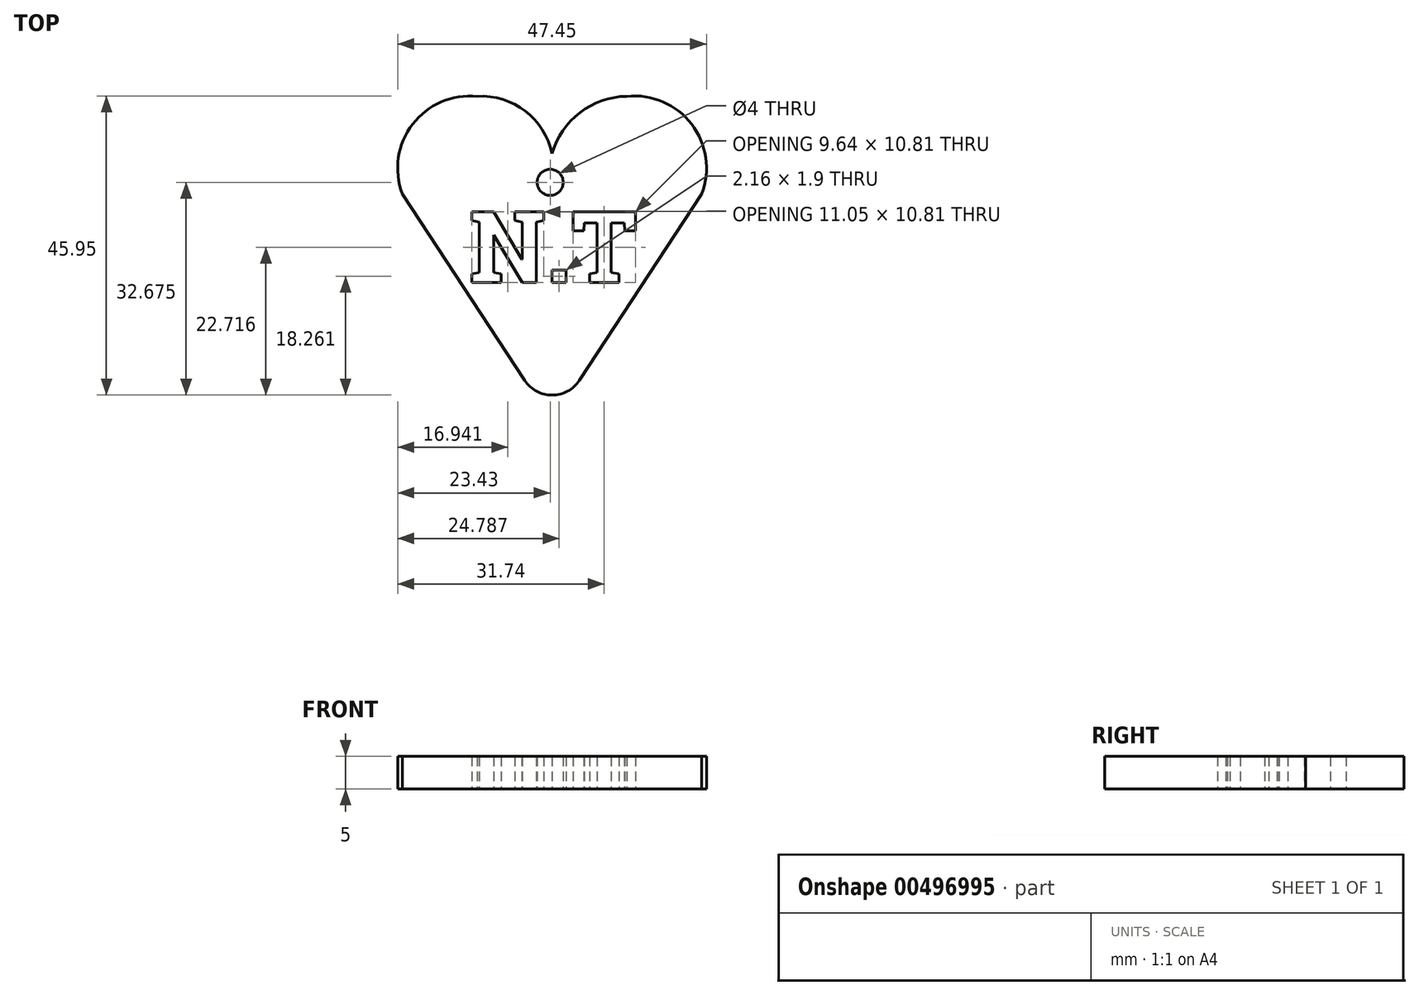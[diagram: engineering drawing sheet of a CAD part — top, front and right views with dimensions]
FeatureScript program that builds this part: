
annotation { "Feature Type Name" : "Feature", "Feature Type Description" : "" }
export const myFeature = defineFeature(function(context is Context, id is Id, definition is map)
    precondition{}
    {
        {
            var Q0;
            Q0=qCreatedBy(makeId("Top.planeOp"),FACE);
            var sketch = newSketch(context, id + "F0", { "sketchPlane" : qUnion([Q0])});
            skPoint(sketch, "E0.startSnap0", {"position": v(-11.21, 33.91) * mm});
            skLineSegment(sketch, "E1", {"start": v(-22.71, 18.92) * mm, "end": v(-3.9, -9.73) * mm});
            skLineSegment(sketch, "E2", {"start": v(23.29, 18.92) * mm, "end": v(4.47, -9.73) * mm});
            skPoint(sketch, "E3.visualSharp", {"position": v(0.29, -16.09) * mm});
            skArc(sketch, "E3.filletArc", {"start": v(-3.9, -9.73) * mm, "mid": v(0.29, -11.98) * mm, "end": v(4.47, -9.73) * mm});
            skArc(sketch, "E4", {"start": v(0.29, 25.1) * mm, "mid": v(-3.83, 31.63) * mm, "end": v(-11.21, 33.91) * mm});
            skArc(sketch, "E5", {"start": v(11.79, 33.91) * mm, "mid": v(4.58, 31.4) * mm, "end": v(0.29, 25.1) * mm});
            skArc(sketch, "E6", {"start": v(-11.21, 33.91) * mm, "mid": v(-21.14, 29.61) * mm, "end": v(-22.71, 18.92) * mm});
            skArc(sketch, "E7", {"start": v(23.29, 18.92) * mm, "mid": v(21.73, 29.63) * mm, "end": v(11.79, 33.91) * mm});
            skText(sketch, "E8", { "text": "N.T", "fontName": "RobotoSlab-Bold.ttf"});
            skCircle(sketch, "E9", {"center": v(0, 20.7) * mm, "radius": 2 * mm});
            skLineSegment(sketch, "E10", {"start": v(0.29, 25.1) * mm, "end": v(0.29, 20.7) * mm});
            const initialGuessF0  = {"E8": [-0.01243, 0.00533, 1, 0, 0.01095]};
            skSetInitialGuess(sketch, initialGuessF0);
            skSolve(sketch);
        }
        {
            var Q0;
            Q0 = qSketchRegion(id + "F0", true);
            extrude(context, id + "F1", {"entities" : qUnion([Q0]), "depth" : 5 * mm, "offsetDistance" : 25 * mm});
        }
    });
